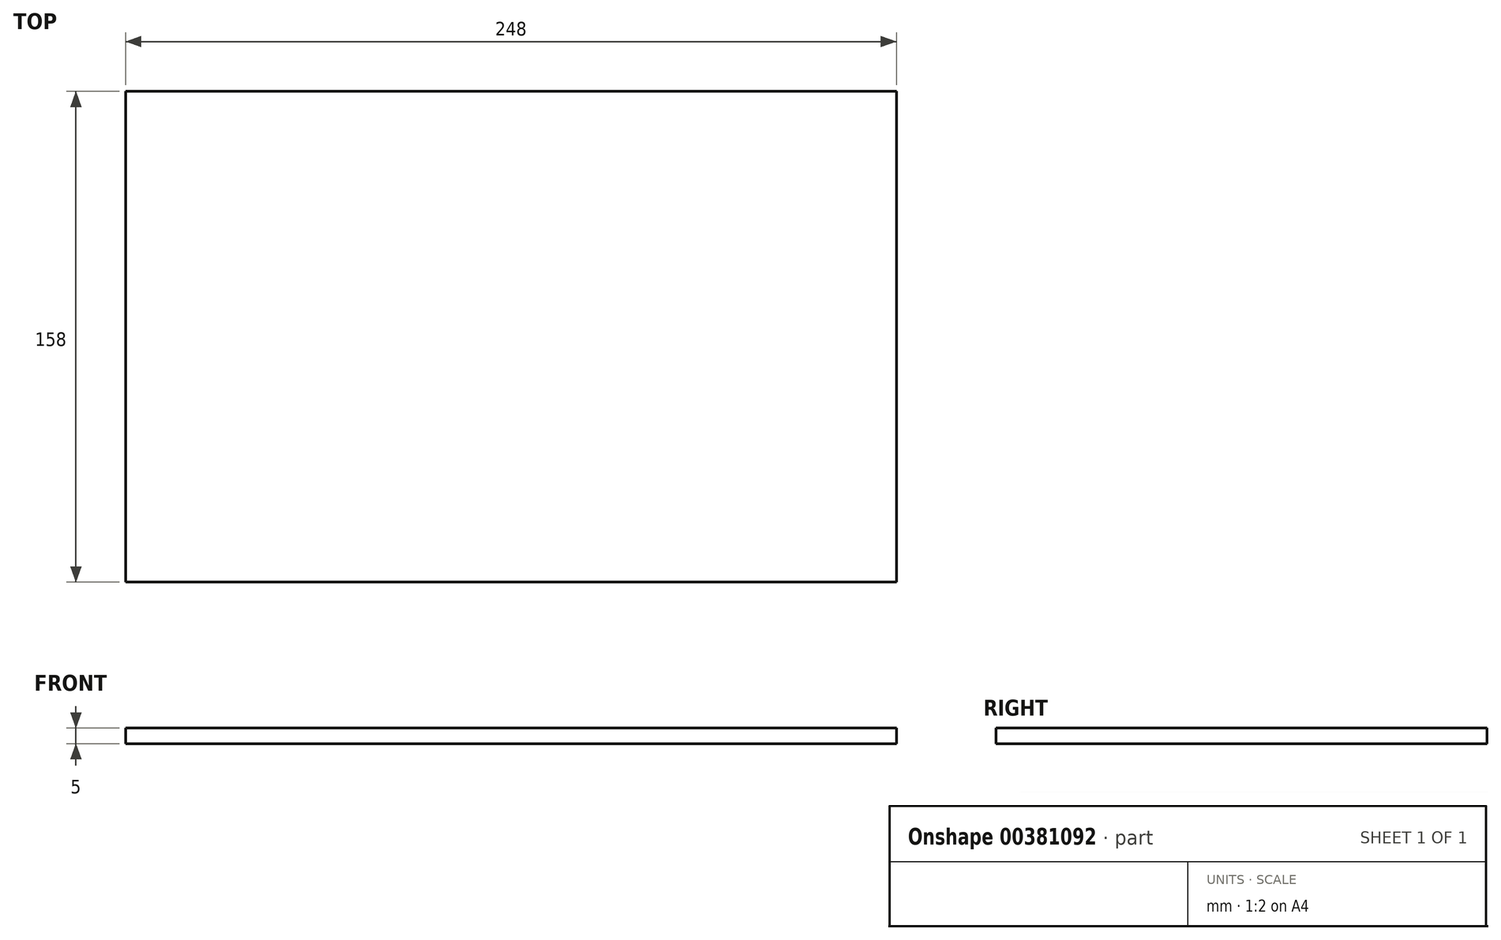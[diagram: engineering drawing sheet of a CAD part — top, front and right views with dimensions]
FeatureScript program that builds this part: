
annotation { "Feature Type Name" : "Feature", "Feature Type Description" : "" }
export const myFeature = defineFeature(function(context is Context, id is Id, definition is map)
    precondition{}
    {
        {
            var Q0;
            Q0=qCreatedBy(makeId("Top.planeOp"),FACE);
            var sketch = newSketch(context, id + "F0", { "sketchPlane" : qUnion([Q0])});
            skLineSegment(sketch, "E0.bottom", {"start": v(-124, 79) * mm, "end": v(124, 79) * mm});
            skLineSegment(sketch, "E0.top", {"start": v(-124, -79) * mm, "end": v(124, -79) * mm});
            skLineSegment(sketch, "E0.left", {"start": v(-124, 79) * mm, "end": v(-124, -79) * mm});
            skLineSegment(sketch, "E0.right", {"start": v(124, 79) * mm, "end": v(124, -79) * mm});
            skSolve(sketch);
        }
        {
            var Q0;
            Q0=makeQuery(id+"F0.imprint","IMPRINT",FACE,{"disambiguationData":[TD([[makeQuery(id+"F0.imprint","IMPRINT",EDGE,{"derivedFrom":sQuery(id+"F0.wireOp",EDGE,"E0.bottom")}),-1.0]])]});
            extrude(context, id + "F1", {"entities" : qUnion([Q0]), "depth" : 5 * mm});
        }
    });
